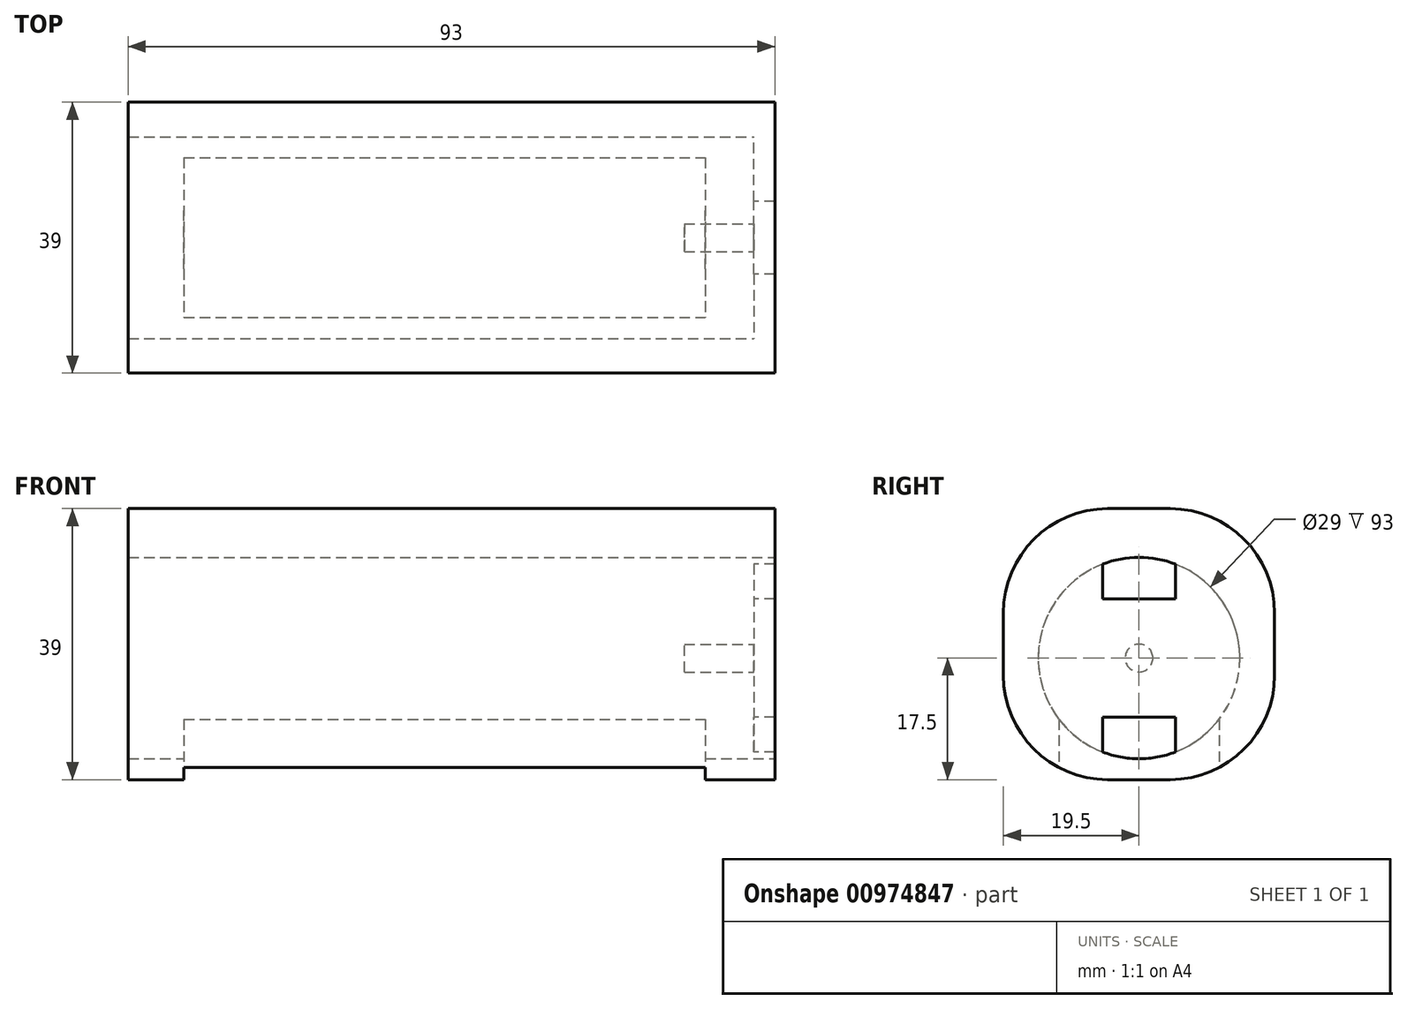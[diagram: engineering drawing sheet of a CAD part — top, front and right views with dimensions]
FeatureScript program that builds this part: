
annotation { "Feature Type Name" : "Feature", "Feature Type Description" : "" }
export const myFeature = defineFeature(function(context is Context, id is Id, definition is map)
    precondition{}
    {
        {
            var Q0;
            Q0=qCreatedBy(makeId("Right.planeOp"),FACE);
            var sketch = newSketch(context, id + "F0", { "sketchPlane" : qUnion([Q0])});
            skCircle(sketch, "E0", {"center": v(0, 0) * mm, "radius": 16.5 * mm});
            skCircle(sketch, "E1", {"center": v(0, 0) * mm, "radius": 14.5 * mm});
            skCircle(sketch, "E2", {"center": v(0, 0) * mm, "radius": 2 * mm});
            skLineSegment(sketch, "E3.bottom", {"start": v(-19.5, 21.5) * mm, "end": v(19.5, 21.5) * mm});
            skLineSegment(sketch, "E3.top", {"start": v(-19.5, -17.5) * mm, "end": v(19.5, -17.5) * mm});
            skLineSegment(sketch, "E3.left", {"start": v(-19.5, 21.5) * mm, "end": v(-19.5, -17.5) * mm});
            skLineSegment(sketch, "E3.right", {"start": v(19.5, 21.5) * mm, "end": v(19.5, -17.5) * mm});
            skLineSegment(sketch, "E4", {"start": v(-5.25, 13.52) * mm, "end": v(-5.25, 8.5) * mm});
            skLineSegment(sketch, "E5", {"start": v(-5.25, 8.5) * mm, "end": v(5.25, 8.5) * mm});
            skLineSegment(sketch, "E6", {"start": v(5.25, 8.5) * mm, "end": v(5.25, 13.52) * mm});
            skLineSegment(sketch, "E7", {"start": v(-5.25, -13.52) * mm, "end": v(-5.25, -8.5) * mm});
            skLineSegment(sketch, "E8", {"start": v(-5.25, -8.5) * mm, "end": v(5.25, -8.5) * mm});
            skLineSegment(sketch, "E9", {"start": v(5.25, -8.5) * mm, "end": v(5.25, -13.52) * mm});
            skLineSegment(sketch, "E10", {"start": v(0, 8.5) * mm, "end": v(0, -8.5) * mm, "construction": true});
            skSolve(sketch);
        }
        {
            var Q0;
            Q0=makeQuery(id+"F0.imprint","IMPRINT",FACE,{"disambiguationData":[TD([[makeQuery(id+"F0.imprint","IMPRINT",EDGE,{"derivedFrom":sQuery(id+"F0.wireOp",EDGE,"E0")}),1.0]])]});
            var Q1;
            Q1=makeQuery(id+"F0.imprint","IMPRINT",FACE,{"disambiguationData":[TD([[makeQuery(id+"F0.imprint","IMPRINT",EDGE,{"derivedFrom":sQuery(id+"F0.wireOp",EDGE,"E3.bottom")}),-1.0]])]});
            extrude(context, id + "F1", {"entities" : qUnion([Q0, Q1]), "oppositeDirection" : true, "depth" : 90 * mm, "offsetDistance" : 25 * mm});
        }
        {
            var Q0;
            Q0=makeQuery(id+"F0.imprint","IMPRINT",FACE,{"disambiguationData":[TD([[makeQuery(id+"F0.imprint","IMPRINT",EDGE,{"derivedFrom":sQuery(id+"F0.wireOp",EDGE,"E2")}),-1.0]])]});
            var Q1;
            {var subQ0=sQuery(id+"F0.wireOp",EDGE,"gJJgYk7n-vuQi-h6Wn-w6bE-JmrjT0mqOlKV");var subQ1=sQuery(id+"F0.wireOp",EDGE,"E0");var subQ2=makeQuery(id+"F0.imprint","INTERSECT",VERTEX,{"disambiguationData":[OD(0.0)],"derivedFrom":[subQ1,subQ0]});Q1=makeQuery(id+"F0.imprint","IMPRINT",FACE,{"disambiguationData":[TD([[makeQuery(id+"F0.imprint","IMPRINT",EDGE,{"disambiguationData":[TD([[subQ2,1.0]])],"derivedFrom":subQ1}),1.0]])]});}
            var Q2;
            {var subQ0=sQuery(id+"F0.wireOp",EDGE,"gJJgYk7n-vuQi-h6Wn-w6bE-JmrjT0mqOlKV");var subQ1=sQuery(id+"F0.wireOp",EDGE,"E0");var subQ2=makeQuery(id+"F0.imprint","INTERSECT",VERTEX,{"disambiguationData":[OD(0.0)],"derivedFrom":[subQ1,subQ0]});Q2=makeQuery(id+"F0.imprint","IMPRINT",FACE,{"disambiguationData":[TD([[makeQuery(id+"F0.imprint","IMPRINT",EDGE,{"disambiguationData":[TD([[subQ2,-1.0]])],"derivedFrom":subQ1}),1.0]])]});}
            var Q3;
            {var subQ0=sQuery(id+"F0.wireOp",EDGE,"e2HM2yV2-Ia9v-laO9-Fszi-1DqRL3o7U61I");var subQ1=sQuery(id+"F0.wireOp",EDGE,"E0");var subQ2=makeQuery(id+"F0.imprint","INTERSECT",VERTEX,{"disambiguationData":[OD(0.0)],"derivedFrom":[subQ1,subQ0]});Q3=makeQuery(id+"F0.imprint","IMPRINT",FACE,{"disambiguationData":[TD([[makeQuery(id+"F0.imprint","IMPRINT",EDGE,{"disambiguationData":[TD([[subQ2,-1.0]])],"derivedFrom":subQ1}),1.0]])]});}
            var Q4;
            {var subQ0=sQuery(id+"F0.wireOp",EDGE,"gJJgYk7n-vuQi-h6Wn-w6bE-JmrjT0mqOlKV");var subQ1=sQuery(id+"F0.wireOp",EDGE,"E0");var subQ2=makeQuery(id+"F0.imprint","INTERSECT",VERTEX,{"disambiguationData":[OD(1.0)],"derivedFrom":[subQ1,subQ0]});Q4=makeQuery(id+"F0.imprint","IMPRINT",FACE,{"disambiguationData":[TD([[makeQuery(id+"F0.imprint","IMPRINT",EDGE,{"disambiguationData":[TD([[subQ2,1.0]])],"derivedFrom":subQ1}),1.0]])]});}
            var Q5;
            Q5=makeQuery(id+"F0.imprint","IMPRINT",FACE,{"disambiguationData":[TD([[makeQuery(id+"F0.imprint","IMPRINT",EDGE,{"derivedFrom":sQuery(id+"F0.wireOp",EDGE,"E2")}),1.0]])]});
            var Q6;
            Q6=makeQuery(id+"F0.imprint","IMPRINT",FACE,{"disambiguationData":[TD([[makeQuery(id+"F0.imprint","IMPRINT",EDGE,{"derivedFrom":sQuery(id+"F0.wireOp",EDGE,"E3.bottom")}),-1.0]])]});
            extrude(context, id + "F2", {"entities" : qUnion([Q0, Q1, Q2, Q3, Q4, Q5, Q6]), "operationType" : NewBodyOperationType.ADD, "depth" : 3 * mm, "offsetDistance" : 25 * mm});
        }
        {
            var Q0;
            {var subQ0=sQuery(id+"F0.wireOp",EDGE,"E3.top");Q0=makeQuery(id+"F2.boolean.opBoolean","MERGE",FACE,{"derivedFrom":[makeQuery(id+"F1.opExtrude","SWEPT_FACE",FACE,{"disambiguationData":[OSD([subQ0])]}),makeQuery(id+"F2.opExtrude","SWEPT_FACE",FACE,{"disambiguationData":[OSD([subQ0])]})]});}
            var sketch = newSketch(context, id + "F3", { "sketchPlane" : qUnion([Q0])});
            skLineSegment(sketch, "E11.0", {"start": v(-82, 11.5) * mm, "end": v(-7, 11.5) * mm});
            skLineSegment(sketch, "E11.1", {"start": v(-82, 11.5) * mm, "end": v(-82, -11.5) * mm});
            skLineSegment(sketch, "E11.2", {"start": v(-82, -11.5) * mm, "end": v(-7, -11.5) * mm});
            skLineSegment(sketch, "E11.3", {"start": v(-7, 11.5) * mm, "end": v(-7, -11.5) * mm});
            skSolve(sketch);
        }
        {
            var Q0;
            Q0=makeQuery(id+"F3.imprint","IMPRINT",FACE,{"disambiguationData":[TD([[makeQuery(id+"F3.imprint","IMPRINT",EDGE,{"derivedFrom":sQuery(id+"F3.wireOp",EDGE,"E11.0")}),-1.0]])]});
            extrude(context, id + "F4", {"entities" : qUnion([Q0]), "operationType" : NewBodyOperationType.REMOVE, "oppositeDirection" : true, "depth" : 21.5 * mm, "offsetDistance" : 25 * mm});
        }
        {
            var Q0;
            Q0=makeQuery(id+"F0.imprint","IMPRINT",FACE,{"disambiguationData":[TD([[makeQuery(id+"F0.imprint","IMPRINT",EDGE,{"derivedFrom":sQuery(id+"F0.wireOp",EDGE,"E2")}),1.0]])]});
            extrude(context, id + "F5", {"entities" : qUnion([Q0]), "operationType" : NewBodyOperationType.ADD, "oppositeDirection" : true, "depth" : 10 * mm, "offsetDistance" : 25 * mm});
        }
        {
            var Q0;
            {var subQ0=sQuery(id+"F0.wireOp",EDGE,"E3.right");var subQ1=sQuery(id+"F0.wireOp",EDGE,"E3.top");Q0=makeQuery(id+"F2.boolean.opBoolean","MERGE",EDGE,{"derivedFrom":[makeQuery(id+"F1.opExtrude","SWEPT_EDGE",EDGE,{"disambiguationData":[OSD([subQ1,subQ0])]}),makeQuery(id+"F2.opExtrude","SWEPT_EDGE",EDGE,{"disambiguationData":[OSD([subQ1,subQ0])]})]});}
            var Q1;
            {var subQ0=sQuery(id+"F0.wireOp",EDGE,"E3.left");var subQ1=sQuery(id+"F0.wireOp",EDGE,"E3.top");Q1=makeQuery(id+"F2.boolean.opBoolean","MERGE",EDGE,{"derivedFrom":[makeQuery(id+"F1.opExtrude","SWEPT_EDGE",EDGE,{"disambiguationData":[OSD([subQ1,subQ0])]}),makeQuery(id+"F2.opExtrude","SWEPT_EDGE",EDGE,{"disambiguationData":[OSD([subQ1,subQ0])]})]});}
            var Q2;
            {var subQ0=sQuery(id+"F0.wireOp",EDGE,"E3.right");var subQ1=sQuery(id+"F0.wireOp",EDGE,"E3.bottom");Q2=makeQuery(id+"F2.boolean.opBoolean","MERGE",EDGE,{"derivedFrom":[makeQuery(id+"F1.opExtrude","SWEPT_EDGE",EDGE,{"disambiguationData":[OSD([subQ1,subQ0])]}),makeQuery(id+"F2.opExtrude","SWEPT_EDGE",EDGE,{"disambiguationData":[OSD([subQ1,subQ0])]})]});}
            var Q3;
            {var subQ0=sQuery(id+"F0.wireOp",EDGE,"E3.left");var subQ1=sQuery(id+"F0.wireOp",EDGE,"E3.bottom");Q3=makeQuery(id+"F2.boolean.opBoolean","MERGE",EDGE,{"derivedFrom":[makeQuery(id+"F1.opExtrude","SWEPT_EDGE",EDGE,{"disambiguationData":[OSD([subQ1,subQ0])]}),makeQuery(id+"F2.opExtrude","SWEPT_EDGE",EDGE,{"disambiguationData":[OSD([subQ1,subQ0])]})]});}
            fillet(context, id + "F6", {"entities" : qUnion([Q0, Q1, Q2, Q3]), "radius" : 15 * mm, "tangentPropagation" : true, "allowEdgeOverflow" : false});
        }
    });
